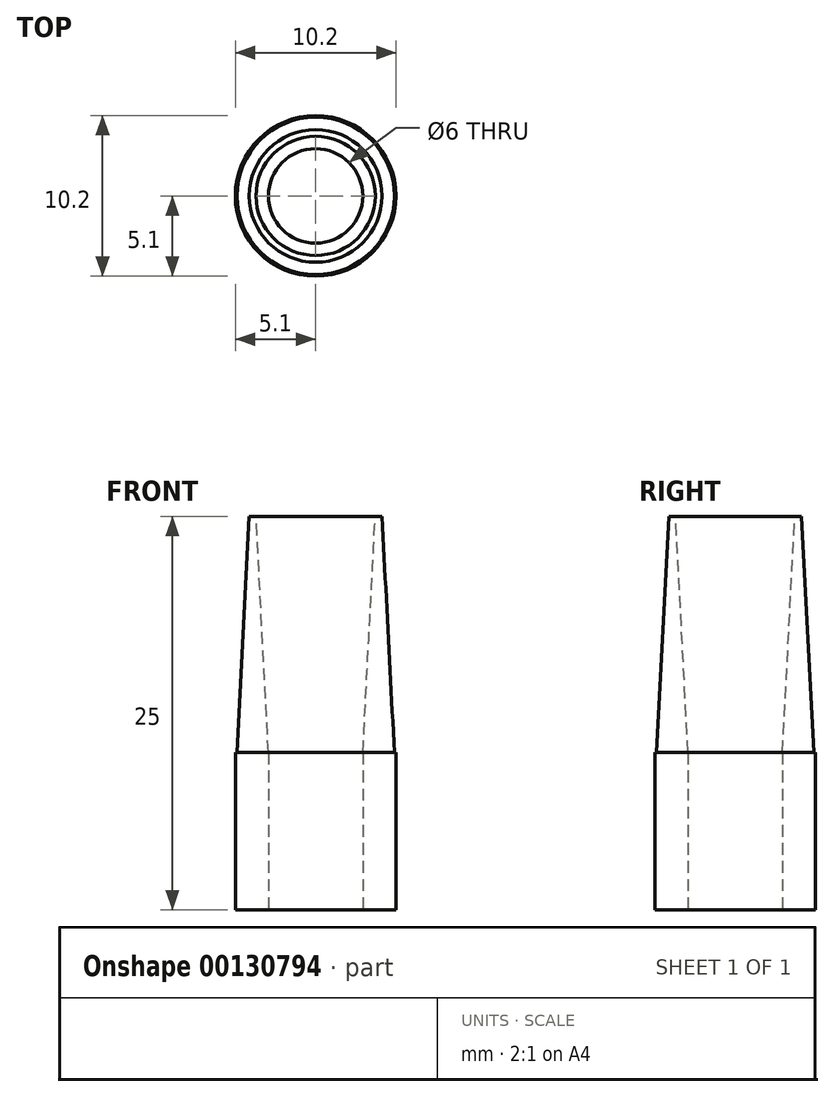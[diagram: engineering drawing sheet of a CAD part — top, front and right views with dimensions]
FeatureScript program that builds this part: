
annotation { "Feature Type Name" : "Feature", "Feature Type Description" : "" }
export const myFeature = defineFeature(function(context is Context, id is Id, definition is map)
    precondition{}
    {
        {
            var Q0;
            Q0=qCreatedBy(makeId("Top.planeOp"),FACE);
            var sketch = newSketch(context, id + "F0", { "sketchPlane" : qUnion([Q0])});
            skCircle(sketch, "E0", {"center": v(0, 0) * mm, "radius": 5.1 * mm});
            skCircle(sketch, "E1", {"center": v(0, 0) * mm, "radius": 3 * mm});
            skSolve(sketch);
        }
        {
            var Q0;
            Q0 = qSketchRegion(id + "F0", true);
            extrude(context, id + "F1", {"entities" : qUnion([Q0]), "depth" : 10 * mm});
        }
        {
            var Q0;
            Q0=makeQuery(id+"F1.opExtrude","CAP_FACE",FACE,{"disambiguationData":[OSD([sQuery(id+"F0.wireOp",EDGE,"E0"),sQuery(id+"F0.wireOp",EDGE,"E1")])],"isStart":false});
            var sketch = newSketch(context, id + "F2", { "sketchPlane" : qUnion([Q0])});
            skCircle(sketch, "E2", {"center": v(0, 0) * mm, "radius": 3 * mm});
            skCircle(sketch, "E3", {"center": v(0, 0) * mm, "radius": 5 * mm});
            skSolve(sketch);
        }
        {
            var Q0;
            Q0 = qSketchRegion(id + "F2", true);
            extrude(context, id + "F3", {"entities" : qUnion([Q0]), "operationType" : NewBodyOperationType.ADD, "depth" : 15 * mm, "hasDraft" : true, "draftAngle" : 3 * degree, "draftPullDirection" : true});
        }
    });
